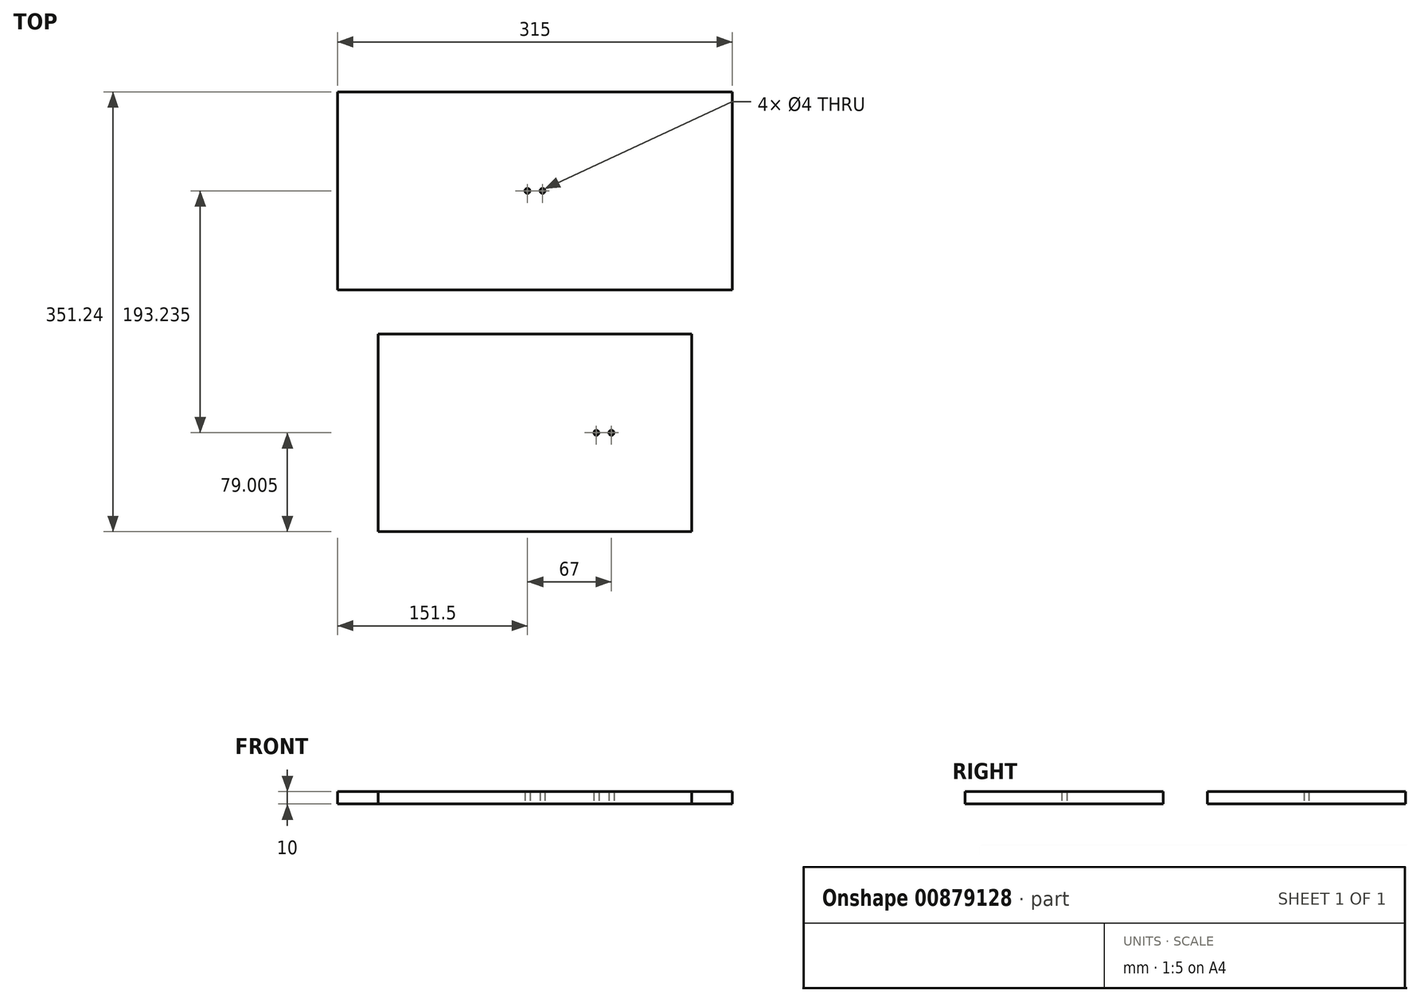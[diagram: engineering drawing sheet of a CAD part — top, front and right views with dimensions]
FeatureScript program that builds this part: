
annotation { "Feature Type Name" : "Feature", "Feature Type Description" : "" }
export const myFeature = defineFeature(function(context is Context, id is Id, definition is map)
    precondition{}
    {
        {
            var Q0;
            Q0=qCreatedBy(makeId("Top.planeOp"),FACE);
            var sketch = newSketch(context, id + "F0", { "sketchPlane" : qUnion([Q0])});
            skLineSegment(sketch, "E0.bottom", {"start": v(-157.5, -79) * mm, "end": v(157.5, -79) * mm});
            skLineSegment(sketch, "E0.top", {"start": v(-157.5, 79) * mm, "end": v(157.5, 79) * mm});
            skLineSegment(sketch, "E0.left", {"start": v(-157.5, -79) * mm, "end": v(-157.5, 79) * mm});
            skLineSegment(sketch, "E0.right", {"start": v(157.5, -79) * mm, "end": v(157.5, 79) * mm});
            skPoint(sketch, "E0.middle", {"position": v(0, 0) * mm});
            skPoint(sketch, "E1.orphan", {"position": v(0, 79) * mm});
            skCircle(sketch, "E2", {"center": v(-6, 0) * mm, "radius": 2 * mm});
            skCircle(sketch, "E3", {"center": v(6, 0) * mm, "radius": 2 * mm});
            skLineSegment(sketch, "E4.bottom", {"start": v(-125, -114.24) * mm, "end": v(125, -114.24) * mm});
            skLineSegment(sketch, "E4.top", {"start": v(-125, -272.24) * mm, "end": v(125, -272.24) * mm});
            skLineSegment(sketch, "E4.left", {"start": v(-125, -114.24) * mm, "end": v(-125, -272.24) * mm});
            skLineSegment(sketch, "E4.right", {"start": v(125, -114.24) * mm, "end": v(125, -272.24) * mm});
            skPoint(sketch, "E4.middle", {"position": v(0, -193.24) * mm});
            skPoint(sketch, "E4.middle.positionSnap0", {"position": v(0, -79) * mm});
            skPoint(sketch, "E4.centerSnap0", {"position": v(0, -79) * mm});
            skCircle(sketch, "E5.MirrorC", {"center": v(49, -193.24) * mm, "radius": 2 * mm});
            skCircle(sketch, "E6.MirrorC", {"center": v(61, -193.24) * mm, "radius": 2 * mm});
            skPoint(sketch, "E7.start.orphan", {"position": v(0, -96.62) * mm});
            skPoint(sketch, "E8.orphan", {"position": v(0, -114.24) * mm});
            skSolve(sketch);
        }
        {
            var Q0;
            Q0 = qSketchRegion(id + "F0", true);
            extrude(context, id + "F1", {"entities" : qUnion([Q0]), "depth" : 10 * mm, "offsetDistance" : 25 * mm});
        }
    });
